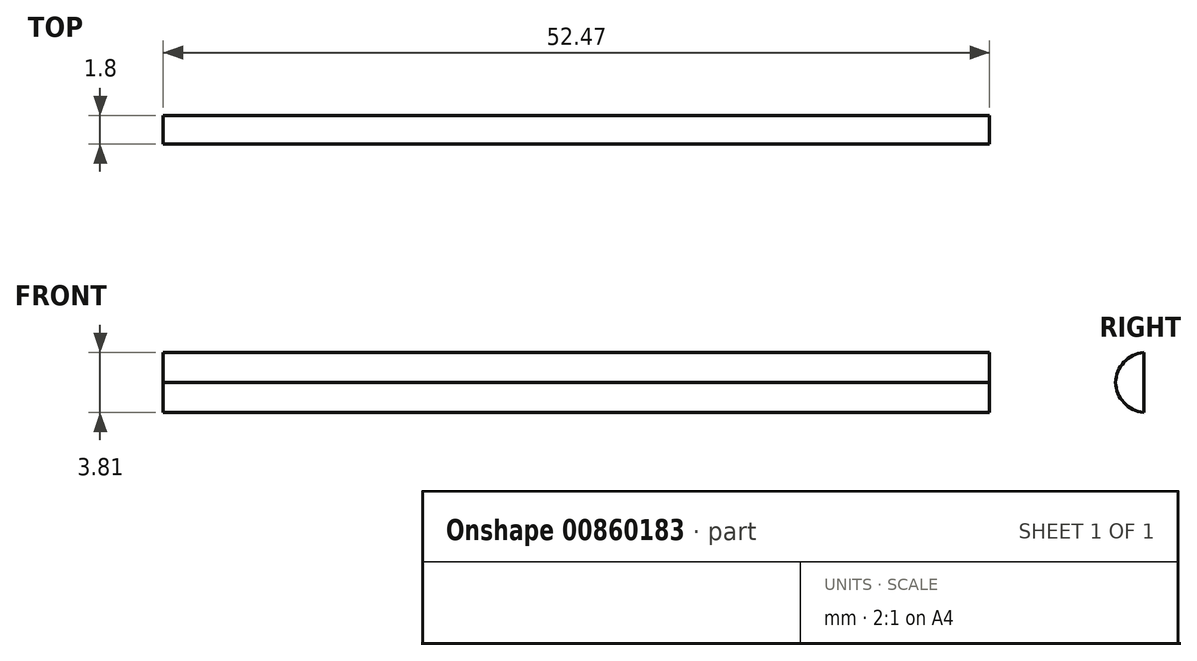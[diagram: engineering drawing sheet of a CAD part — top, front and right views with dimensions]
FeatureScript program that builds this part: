
annotation { "Feature Type Name" : "Feature", "Feature Type Description" : "" }
export const myFeature = defineFeature(function(context is Context, id is Id, definition is map)
    precondition{}
    {
        {
            var Q0;
            Q0=qCreatedBy(makeId("Front.planeOp"),FACE);
            var sketch = newSketch(context, id + "F0", { "sketchPlane" : qUnion([Q0])});
            skLineSegment(sketch, "E0.bottom", {"start": v(-42.8, 32.2) * mm, "end": v(9.67, 32.2) * mm});
            skLineSegment(sketch, "E0.top", {"start": v(-42.8, 28.4) * mm, "end": v(9.67, 28.4) * mm});
            skLineSegment(sketch, "E0.left", {"start": v(-42.8, 32.2) * mm, "end": v(-42.8, 28.4) * mm});
            skLineSegment(sketch, "E0.right", {"start": v(9.67, 32.2) * mm, "end": v(9.67, 28.4) * mm});
            skSolve(sketch);
        }
        {
            var Q0;
            Q0=makeQuery(id+"F0.imprint","IMPRINT",FACE,{"disambiguationData":[TD([[makeQuery(id+"F0.imprint","IMPRINT",EDGE,{"derivedFrom":sQuery(id+"F0.wireOp",EDGE,"E0.bottom")}),-1.0]])]});
            extrude(context, id + "F1", {"entities" : qUnion([Q0]), "depth" : 1.8 * mm, "offsetDistance" : 25 * mm});
        }
        {
            var Q0;
            Q0=makeQuery(id+"F1.opExtrude","CAP_EDGE",EDGE,{"disambiguationData":[OSD([sQuery(id+"F0.wireOp",EDGE,"E0.bottom")])],"isStart":false});
            var Q1;
            Q1=makeQuery(id+"F1.opExtrude","CAP_EDGE",EDGE,{"disambiguationData":[OSD([sQuery(id+"F0.wireOp",EDGE,"E0.top")])],"isStart":false});
            fillet(context, id + "F2", {"entities" : qUnion([Q0, Q1]), "radius" : 2 * mm, "tangentPropagation" : true, "allowEdgeOverflow" : false});
        }
    });
